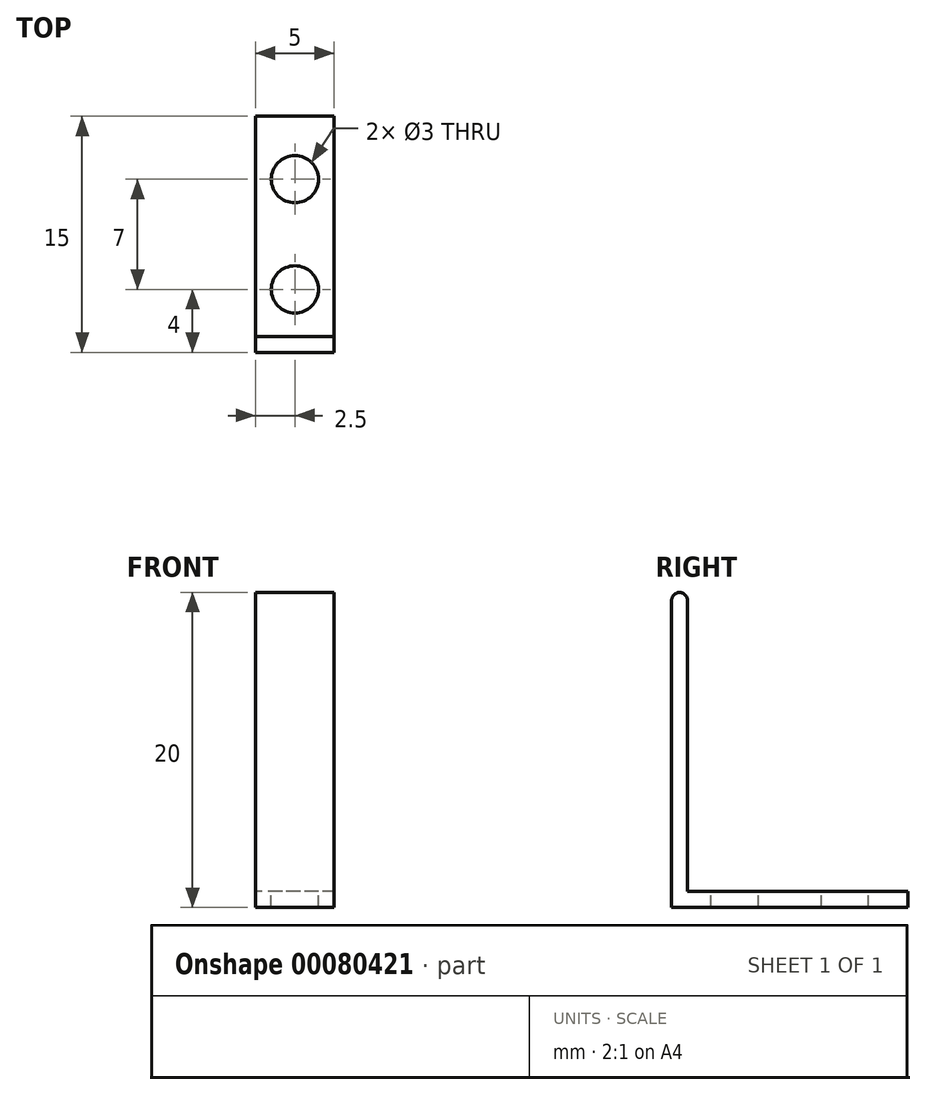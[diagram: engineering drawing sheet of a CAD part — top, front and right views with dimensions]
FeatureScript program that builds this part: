
annotation { "Feature Type Name" : "Feature", "Feature Type Description" : "" }
export const myFeature = defineFeature(function(context is Context, id is Id, definition is map)
    precondition{}
    {
        {
            var Q0;
            Q0=qCreatedBy(makeId("Right.planeOp"),FACE);
            var sketch = newSketch(context, id + "F0", { "sketchPlane" : qUnion([Q0])});
            skLineSegment(sketch, "E0", {"start": v(7.5, 0) * mm, "end": v(-7.5, 0) * mm});
            skLineSegment(sketch, "E1", {"start": v(-7.5, 0) * mm, "end": v(-7.5, 20) * mm});
            skLineSegment(sketch, "E2", {"start": v(-6.5, 20) * mm, "end": v(-7.5, 20) * mm});
            skLineSegment(sketch, "E3", {"start": v(-6.5, 20) * mm, "end": v(-6.5, 1) * mm});
            skLineSegment(sketch, "E4", {"start": v(-6.5, 1) * mm, "end": v(7.5, 1) * mm});
            skLineSegment(sketch, "E5", {"start": v(7.5, 1) * mm, "end": v(7.5, 0) * mm});
            skPoint(sketch, "E6", {"position": v(0, 0) * mm});
            skSolve(sketch);
        }
        {
            var Q0;
            Q0 = qSketchRegion(id + "F0", true);
            extrude(context, id + "F1", {"entities" : qUnion([Q0]), "endBound" : BoundingType.SYMMETRIC, "depth" : 5 * mm});
        }
        {
            var Q0;
            Q0=makeQuery(id+"F1.opExtrude","SWEPT_FACE",FACE,{"disambiguationData":[OSD([sQuery(id+"F0.wireOp",EDGE,"E4")])]});
            var sketch = newSketch(context, id + "F2", { "sketchPlane" : qUnion([Q0])});
            skCircle(sketch, "E7", {"center": v(0, 3.5) * mm, "radius": 1.5 * mm});
            skCircle(sketch, "E8.MirrorC", {"center": v(0, -3.5) * mm, "radius": 1.5 * mm});
            skSolve(sketch);
        }
        {
            var Q0;
            Q0 = qSketchRegion(id + "F2", true);
            extrude(context, id + "F3", {"entities" : qUnion([Q0]), "operationType" : NewBodyOperationType.REMOVE, "endBound" : BoundingType.UP_TO_NEXT, "oppositeDirection" : true, "depth" : 25 * mm});
        }
        {
            var Q0;
            Q0=makeQuery(id+"F1.opExtrude","SWEPT_EDGE",EDGE,{"disambiguationData":[OSD([sQuery(id+"F0.wireOp",EDGE,"E2"),sQuery(id+"F0.wireOp",EDGE,"E3")])]});
            var Q1;
            Q1=makeQuery(id+"F1.opExtrude","SWEPT_EDGE",EDGE,{"disambiguationData":[OSD([sQuery(id+"F0.wireOp",EDGE,"E1"),sQuery(id+"F0.wireOp",EDGE,"E2")])]});
            fillet(context, id + "F4", {"entities" : qUnion([Q0, Q1]), "radius" : 0.5 * mm, "tangentPropagation" : true, "allowEdgeOverflow" : false});
        }
    });
